FCSTD DOCUMENT  (FreeCAD 1.0R39285 (Git))
Label: Mover
License: All rights reserved
LicenseURL: https://en.wikipedia.org/wiki/All_rights_reserved
objects: App::Link×59, App::FeaturePython×47, Part::Feature×43, Part::FeaturePython×8, App::Part×4, Assembly::AssemblyLink×4, Assembly::JointGroup×2, Assembly::AssemblyObject×2, App::DocumentObjectGroup×1
note: 51 computed .brp shape members not serialized (recipe doc carries the construction recipe); baked Part::Feature solids carry a one-line shape summary decoded from their .brp
EXTERNAL_REF file=Heberteile.FCStd obj=Body001
EXTERNAL_REF file=Heberteile.FCStd obj=Body
EXTERNAL_REF file=Heberteile.FCStd obj=Body003
EXTERNAL_REF file=Heberteile.FCStd obj=Body002
EXTERNAL_REF file=Heberteile.FCStd obj=Body005
EXTERNAL_REF file=Heberteile.FCStd obj=Body006
EXTERNAL_REF file=Heberteile.FCStd obj=Body007

FEATURE [App::Link] B_Steppersledge_basic  label="B-Steppersledge basic"
  LinkPlacement = pos=(-30.1438,29,574.644) rot=(0.707107,0,-0.707107;3.14159rad)
  LinkedObject = -> <external Heberteile.FCStd>#Body001
  Placement = pos=(-30.1438,29,574.644) rot=(0.707107,0,-0.707107;3.14159rad)
FEATURE [App::Link] B_Steppersledge_Switch  label="B-Steppersledge Switch"
  LinkPlacement = pos=(30.8669,-32.6406,574.644) rot=(0,1,0;1.5708rad)
  LinkedObject = -> <external Heberteile.FCStd>#Body
  Placement = pos=(30.8669,-32.6406,574.644) rot=(0,1,0;1.5708rad)
FEATURE [App::Link] B_SlideBearing  label="B-Slide Bearing R"
  LinkPlacement = pos=(-29.9938,-1.19447e-11,401.144) rot=(-0.707107,0,0.707107;3.14159rad)
  LinkedObject = -> <external Heberteile.FCStd>#Body003
  Placement = pos=(-29.9938,-1.19447e-11,401.144) rot=(-0.707107,0,0.707107;3.14159rad)
FEATURE [App::Link] B_Sheetwasher  label="B-Mount Washer R"
  LinkPlacement = pos=(-26.1438,-3.388e-12,195.644) rot=(0.707107,0,-0.707107;3.14159rad)
  LinkedObject = -> <external Heberteile.FCStd>#Body002
  Placement = pos=(-26.1438,-3.388e-12,195.644) rot=(0.707107,0,-0.707107;3.14159rad)
FEATURE [Part::Feature] Part__Feature  label="23HS45-4204S"
  shape: bbox 1.354 x 20 x 1.354 mm, 4 faces (baked)
FEATURE [Part::Feature] Part__Feature001  label="23HS45-4204S001"
  shape: bbox 1.354 x 20 x 1.354 mm, 4 faces (baked)
FEATURE [Part::Feature] Part__Feature002  label="23HS45-4204S002"
  shape: bbox 1.354 x 20 x 1.354 mm, 4 faces (baked)
FEATURE [Part::Feature] Part__Feature003  label="23HS45-4204S003"
  shape: bbox 8 x 0.5 x 10.5 mm, 12 faces (baked)
FEATURE [Part::Feature] Part__Feature004  label="23HS45-4204S004"
  shape: bbox 57 x 78.2 x 137 mm, 432 faces (baked)
FEATURE [Part::Feature] Part__Feature005  label="23HS45-4204S005"
  shape: bbox 1.354 x 20 x 1.354 mm, 4 faces (baked)
FEATURE [App::Part] _3HS45_4204S  label="23HS45-4204S006"
  Group = -> [Part__Feature,Part__Feature001,Part__Feature002,Part__Feature003,Part__Feature004,Part__Feature005]
  Origin = -> Origin
FEATURE [Part::Feature] Part__Feature006  label="DM542T(V4.0)"
  shape: bbox 1.24 x 1.535 x 2.051 mm, 6 faces (baked)
FEATURE [Part::Feature] Part__Feature007  label="DM542T(V4.0)001"
  shape: bbox 6.47 x 10.45 x 10.4 mm, 69 faces (baked)
FEATURE [Part::Feature] Part__Feature008  label="DM542T(V4.0)002"
  shape: bbox 1.24 x 1.535 x 2.051 mm, 6 faces (baked)
FEATURE [Part::Feature] Part__Feature009  label="DM542T(V4.0)003"
  shape: bbox 19.2 x 10.45 x 10.4 mm, 168 faces (baked)
FEATURE [Part::Feature] Part__Feature010  label="DM542T(V4.0)004"
  shape: bbox 1.24 x 1.535 x 2.051 mm, 6 faces (baked)
FEATURE [Part::Feature] Part__Feature011  label="DM542T(V4.0)005"
  shape: bbox 24 x 13.06 x 13 mm, 168 faces (baked)
FEATURE [Part::Feature] Part__Feature012  label="DM542T(V4.0)006"
  shape: bbox 1.24 x 1.535 x 2.051 mm, 6 faces (baked)
FEATURE [Part::Feature] Part__Feature013  label="DM542T(V4.0)007"
  shape: bbox 1.24 x 1.535 x 2.051 mm, 6 faces (baked)
FEATURE [Part::Feature] Part__Feature014  label="DM542T(V4.0)008"
  shape: bbox 122 x 25.5 x 79.9 mm, 393 faces (baked)
FEATURE [App::Part] DM542T_V4_0_  label="DM542T(V4.0)009"
  Group = -> [Part__Feature006,Part__Feature007,Part__Feature008,Part__Feature009,Part__Feature010,Part__Feature011,Part__Feature012,Part__Feature013,Part__Feature014]
  Origin = -> Origin002
FEATURE [Part::Feature] Part__Feature016  label="Microswitch 20mm001"
  shape: bbox 3.3 x 1.3 x 2 mm, 8 faces (baked)
FEATURE [Part::Feature] Part__Feature017  label="Microswitch 20mm002"
  shape: bbox 4.6 x 9.15 x 18.7 mm, 30 faces (baked)
FEATURE [Part::Feature] Part__Feature018  label="Microswitch 20mm003"
  shape: bbox 3.1 x 3.6 x 0.5 mm, 9 faces (baked)
FEATURE [Part::Feature] Part__Feature019  label="Microswitch 20mm004"
  shape: bbox 3.1 x 3.6 x 0.5 mm, 9 faces (baked)
FEATURE [Part::Feature] Part__Feature020  label="Microswitch 20mm005"
  shape: bbox 3.1 x 3.6 x 0.5 mm, 9 faces (baked)
FEATURE [Part::Feature] Part__Feature021  label="Microswitch 20mm006"
  shape: bbox 3.4 x 4.979 x 4.979 mm, 6 faces (baked)
FEATURE [Part::Feature] Part__Feature022  label="base plate"
  Placement = pos=(40.6975,42.3791,107.628) rot=(0,0,1;0rad)
  shape: bbox 133.6 x 40.07 x 89.98 mm, 156 faces (baked)
FEATURE [Part::Feature] Part__Feature023  label="carrier plate"
  Placement = pos=(40.6975,172.684,107.628) rot=(0,0,1;3.14159rad)
  shape: bbox 64 x 43.47 x 38.95 mm, 106 faces (baked)
FEATURE [Part::Feature] Part__Feature024  label="upper lifting arm"
  Placement = pos=(123.841,140.552,107.628) rot=(0,0,1;2.8646rad)
  shape: bbox 166 x 65.79 x 28 mm, 172 faces (baked)
FEATURE [Part::Feature] Part__Feature025  label="top lifting arm"
  Placement = pos=(123.841,81.5103,107.628) rot=(-0.138054,0.990425,0;3.14159rad)
  shape: bbox 166 x 65.79 x 38 mm, 172 faces (baked)
FEATURE [Part::Feature] Part__Feature026  label="upper left lifting arm"
  Placement = pos=(-42.4461,140.552,107.628) rot=(0.990425,0.138054,0;3.14159rad)
  shape: bbox 165.5 x 66.16 x 28 mm, 206 faces (baked)
FEATURE [Part::Feature] Part__Feature027  label="top left lifting arm"
  Placement = pos=(-42.4461,81.5103,107.628) rot=(0,0,-1;0.276992rad)
  shape: bbox 165.5 x 66.16 x 38 mm, 206 faces (baked)
FEATURE [Part::Feature] Part__Feature028  label="top pins"
  Placement = pos=(27.4475,150.684,126.628) rot=(0.706529,-0.040404,-0.706529;3.22236rad)
  shape: bbox 11.83 x 11.83 x 46 mm, 15 faces (baked)
FEATURE [Part::Feature] Part__Feature029  label="bottom pins"
  Placement = pos=(27.4475,71.3791,131.628) rot=(-0.281558,0.917306,0.281558;1.657rad)
  shape: bbox 11.69 x 11.69 x 56 mm, 15 faces (baked)
FEATURE [Part::Feature] Part__Feature030  label="top pins001"
  Placement = pos=(53.9475,150.684,126.628) rot=(0.704441,0.086746,-0.704441;2.96853rad)
  shape: bbox 11.55 x 11.55 x 46 mm, 15 faces (baked)
FEATURE [Part::Feature] Part__Feature031  label="bottom pins001"
  Placement = pos=(53.9475,71.3791,131.628) rot=(0.632857,-0.446075,-0.632857;3.98076rad)
  shape: bbox 11.21 x 11.21 x 56 mm, 15 faces (baked)
FEATURE [Part::Feature] Part__Feature032  label="drive screw"
  Placement = pos=(-121.025,111.031,107.628) rot=(0.687636,-0.233053,0.687636;3.59952rad)
  shape: bbox 361.7 x 22.9 x 16.1 mm, 155 faces (baked)
FEATURE [Part::Feature] Part__Feature033  label="drive trunnion"
  Placement = pos=(202.42,111.031,107.628) rot=(0,-1,0;1.5708rad)
  shape: bbox 21.48 x 18 x 18 mm, 27 faces (baked)
FEATURE [Part::Feature] Part__Feature034  label="stationary trunnion"
  Placement = pos=(-103.025,111.031,107.628) rot=(0,-1,0;1.5708rad)
  shape: bbox 18 x 18 x 18 mm, 14 faces (baked)
FEATURE [Part::Feature] Part__Feature035  label="turunnion pins"
  Placement = pos=(-112.025,111.031,126.628) rot=(-0.675166,0.297157,0.675166;2.5639rad)
  shape: bbox 15 x 15 x 16 mm, 9 faces (baked)
FEATURE [Part::Feature] Part__Feature036  label="turunnion pins001"
  Placement = pos=(-112.025,111.031,88.6277) rot=(-0.079144,-0.993716,-0.079144;1.5771rad)
  shape: bbox 15 x 15 x 16 mm, 9 faces (baked)
FEATURE [Part::Feature] Part__Feature037  label="turunnion pins002"
  Placement = pos=(193.42,111.031,88.6277) rot=(-0.079144,-0.993716,-0.079144;1.5771rad)
  shape: bbox 15 x 15 x 16 mm, 9 faces (baked)
FEATURE [Part::Feature] Part__Feature038  label="turunnion pins003"
  Placement = pos=(193.42,111.031,126.628) rot=(0.706974,-0.019411,-0.706974;3.18041rad)
  shape: bbox 15 x 15 x 16 mm, 9 faces (baked)
FEATURE [Part::Feature] Part__Feature039  label="snap ring"
  Placement = pos=(53.9475,150.684,87.8777) rot=(0,0,-1;0.735498rad)
  shape: bbox 10.43 x 10.13 x 0.5 mm, 22 faces (baked)
FEATURE [Part::Feature] Part__Feature040  label="snap ring001"
  Placement = pos=(27.4475,150.684,87.8777) rot=(0,0,-1;0.735498rad)
  shape: bbox 10.43 x 10.13 x 0.5 mm, 22 faces (baked)
FEATURE [Part::Feature] Part__Feature041  label="snap ring002"
  Placement = pos=(53.9475,71.3791,83.3777) rot=(0.933139,-0.359516,0;3.14159rad)
  shape: bbox 10.43 x 10.13 x 0.5 mm, 22 faces (baked)
FEATURE [Part::Feature] Part__Feature042  label="snap ring003"
  Placement = pos=(27.4475,71.3791,82.8777) rot=(0,0,-1;0.735498rad)
  shape: bbox 10.43 x 10.13 x 0.5 mm, 22 faces (baked)
FEATURE [App::Part] lifting_jack_assembley  label="lifting jack assembley"
  Group = -> [Part__Feature022,Part__Feature023,Part__Feature024,Part__Feature025,Part__Feature026,Part__Feature027,Part__Feature028,Part__Feature029,Part__Feature030,Part__Feature031,Part__Feature032,Part__Feature033,Part__Feature034,Part__Feature035,Part__Feature036,Part__Feature037,Part__Feature038,Part__Feature039,Part__Feature040,Part__Feature041,Part__Feature042]
  Origin = -> Origin004
  Placement = pos=(267.1,-82.7,87.3) rot=(0,-1,0;3.14159rad)
FEATURE [App::Link] _3HS45_4204S006  label="23HS45-4204S007"
  LinkedObject = -> _3HS45_4204S
FEATURE [App::FeaturePython] GroundedJoint  # Assembly grounded joint (typed FeaturePython)
  ObjectToGround = -> _3HS45_4204S006
FEATURE [App::FeaturePython] Joint  label="Distance"  # Assembly joint (typed FeaturePython)
  Activated = true
  AngleMax = 0
  AngleMin = 0
  Detach1 = false
  Detach2 = false
  Distance = 0
  Distance2 = 0
  EnableAngleMax = false
  EnableAngleMin = false
  EnableLengthMax = false
  EnableLengthMin = false
  JointType = 5 (Distance)
  LengthMax = 0
  LengthMin = 0
  Placement1 = pos=(461.644,29,-11.5732) rot=(0,1,0;1.5708rad)
  Placement2 = pos=(-0.00133091,0.00678875,113) rot=(0,0,1;0rad)
  Reference1 = -> Assembly [B_Steppersledge_Switch.Face43,B_Steppersledge_Switch.Face43]
  Reference2 = -> Assembly [_3HS45_4204S006.Part__Feature004.Face286,_3HS45_4204S006.Part__Feature004.Vertex39]
FEATURE [App::FeaturePython] Joint001  label="Distance001"  # Assembly joint (typed FeaturePython)
  Activated = true
  AngleMax = 0
  AngleMin = 0
  Detach1 = false
  Detach2 = false
  Distance = 0
  Distance2 = 0
  EnableAngleMax = false
  EnableAngleMin = false
  EnableLengthMax = false
  EnableLengthMin = false
  JointType = 5 (Distance)
  LengthMax = 0
  LengthMin = 0
  Placement1 = pos=(-0.00133091,0.00678875,113) rot=(0,0,1;0rad)
  Placement2 = pos=(461.644,29,-11.5732) rot=(0,1,0;1.5708rad)
  Reference1 = -> Assembly [_3HS45_4204S006.Part__Feature004.Face286,_3HS45_4204S006.Part__Feature004.Vertex48]
  Reference2 = -> Assembly [B_Steppersledge_basic.Face51,B_Steppersledge_basic.Face51]
FEATURE [App::FeaturePython] Joint002  label="Slider"  # Assembly joint (typed FeaturePython)
  Activated = true
  AngleMax = 0
  AngleMin = 0
  Detach1 = false
  Detach2 = false
  Distance = 0
  Distance2 = 0
  EnableAngleMax = false
  EnableAngleMin = false
  EnableLengthMax = false
  EnableLengthMin = false
  JointType = 3 (Slider)
  LengthMax = 0
  LengthMin = 0
  Placement1 = pos=(-23.57,-23.57,110.25) rot=(0,0,1;0rad)
  Placement2 = pos=(460.644,52.57,-6.57381) rot=(0,1,0;1.5708rad)
  Reference1 = -> Assembly [_3HS45_4204S006.Part__Feature004.Face20,_3HS45_4204S006.Part__Feature004.Face20]
  Reference2 = -> Assembly [B_Steppersledge_basic.Face48,B_Steppersledge_basic.Face48]
FEATURE [App::FeaturePython] Joint003  label="Slider001"  # Assembly joint (typed FeaturePython)
  Activated = true
  AngleMax = 0
  AngleMin = 0
  Detach1 = false
  Detach2 = false
  Distance = 0
  Distance2 = 0
  EnableAngleMax = false
  EnableAngleMin = false
  EnableLengthMax = false
  EnableLengthMin = false
  JointType = 3 (Slider)
  LengthMax = 0
  LengthMin = 0
  Placement1 = pos=(459.644,5.43,-6.57381) rot=(0,1,0;1.5708rad)
  Placement2 = pos=(-23.57,23.57,110.25) rot=(0,0,1;0rad)
  Reference1 = -> Assembly [B_Steppersledge_basic.Edge90,B_Steppersledge_basic.Edge90]
  Reference2 = -> Assembly [_3HS45_4204S006.Part__Feature004.Face23,_3HS45_4204S006.Part__Feature004.Face23]
FEATURE [App::FeaturePython] Joint004  label="Slider002"  # Assembly joint (typed FeaturePython)
  Activated = true
  AngleMax = 0
  AngleMin = 0
  Detach1 = false
  Detach2 = false
  Distance = 0
  Distance2 = 0
  EnableAngleMax = false
  EnableAngleMin = false
  EnableLengthMax = false
  EnableLengthMin = false
  JointType = 3 (Slider)
  LengthMax = 0
  LengthMin = 0
  Placement1 = pos=(460.644,52.57,-6.57381) rot=(0,1,0;1.5708rad)
  Placement2 = pos=(23.57,23.57,110.25) rot=(0,0,1;0rad)
  Reference1 = -> Assembly [B_Steppersledge_Switch.Face64,B_Steppersledge_Switch.Face64]
  Reference2 = -> Assembly [_3HS45_4204S006.Part__Feature004.Face22,_3HS45_4204S006.Part__Feature004.Face22]
FEATURE [App::FeaturePython] Joint005  label="Slider003"  # Assembly joint (typed FeaturePython)
  Activated = true
  AngleMax = 0
  AngleMin = 0
  Detach1 = false
  Detach2 = false
  Distance = 0
  Distance2 = 0
  EnableAngleMax = false
  EnableAngleMin = false
  EnableLengthMax = false
  EnableLengthMin = false
  JointType = 3 (Slider)
  LengthMax = 0
  LengthMin = 0
  Placement1 = pos=(23.57,-23.57,110.25) rot=(0,0,1;0rad)
  Placement2 = pos=(460.644,5.43,-6.57381) rot=(0,1,0;1.5708rad)
  Reference1 = -> Assembly [_3HS45_4204S006.Part__Feature004.Face21,_3HS45_4204S006.Part__Feature004.Face21]
  Reference2 = -> Assembly [B_Steppersledge_Switch.Face63,B_Steppersledge_Switch.Face63]
FEATURE [Part::FeaturePython] Nut  label="M5-Mutter"  # WARN: FeaturePython — macro-defined, semantics opaque (R4)
  Diameter = 1
  Invert = false
  LeftHanded = false
  MatchOuter = false
  OffsetAngle = 0
  Placement = pos=(-12.9,0,-58.2) rot=(0,0,1;0rad)
  Thread = false
  Type = 33
FEATURE [Part::FeaturePython] Nut001  label="M2.5-Mutter"  # WARN: FeaturePython — macro-defined, semantics opaque (R4)
  Diameter = 3
  Invert = false
  LeftHanded = false
  MatchOuter = false
  OffsetAngle = 0
  Placement = pos=(0,0,-57.3) rot=(0,0,1;0rad)
  Thread = false
  Type = 31
FEATURE [Part::FeaturePython] Washer  label="M5-Scheibe"  # WARN: FeaturePython — macro-defined, semantics opaque (R4)
  Diameter = 6
  Invert = false
  MatchOuter = false
  OffsetAngle = 0
  Placement = pos=(-12.4,0,-51.8) rot=(0,0,1;0rad)
  Type = 8
FEATURE [Part::FeaturePython] Washer001  label="M2.5-Scheibe"  # WARN: FeaturePython — macro-defined, semantics opaque (R4)
  Diameter = 3
  Invert = false
  MatchOuter = false
  OffsetAngle = 0
  Placement = pos=(0,0,-51.5) rot=(0,0,1;0rad)
  Type = 8
FEATURE [Part::FeaturePython] Screw003  label="M5x12-Schraube"  # WARN: FeaturePython — macro-defined, semantics opaque (R4)
  Diameter = 5
  Invert = false
  LeftHanded = false
  Length = 2
  LengthCustom = 12
  MatchOuter = false
  OffsetAngle = 0
  Placement = pos=(-13.1,0,-36.9) rot=(0,0,1;0rad)
  Thread = false
  Type = 53
FEATURE [App::Link] M5x12_Schraube  label="M5x12-Schraube-Stepper-001"
  LinkPlacement = pos=(-23.57,23.57,108) rot=(1,0,0;3.14159rad)
  LinkedObject = -> Screw003
  Placement = pos=(-23.57,23.57,108) rot=(1,0,0;3.14159rad)
FEATURE [App::Link] M5x12_Schraube001  label="M5x12-Schraube-Stepper-002"
  LinkPlacement = pos=(23.57,23.57,108) rot=(1,0,0;3.14159rad)
  LinkedObject = -> Screw003
  Placement = pos=(23.57,23.57,108) rot=(1,0,0;3.14159rad)
FEATURE [App::Link] M5x12_Schraube002  label="M5x12-Schraube-Stepper-003"
  LinkPlacement = pos=(23.57,-23.57,108) rot=(1,0,0;3.14159rad)
  LinkedObject = -> Screw003
  Placement = pos=(23.57,-23.57,108) rot=(1,0,0;3.14159rad)
FEATURE [App::Link] M5x12_Schraube003  label="M5x12-Schraube-Stepper-004"
  LinkPlacement = pos=(-23.57,-23.57,108) rot=(1,0,0;3.14159rad)
  LinkedObject = -> Screw003
  Placement = pos=(-23.57,-23.57,108) rot=(1,0,0;3.14159rad)
FEATURE [App::Link] M5_Scheibe  label="M5-Scheibe-Stepper-001"
  LinkPlacement = pos=(-23.57,23.57,115) rot=(0,0,1;0rad)
  LinkedObject = -> Washer
  Placement = pos=(-23.57,23.57,115) rot=(0,0,1;0rad)
FEATURE [App::Link] M5_Scheibe001  label="M5-Scheibe-Stepper-003"
  LinkPlacement = pos=(23.57,-23.57,115) rot=(0,0,1;3.14159rad)
  LinkedObject = -> Washer
  Placement = pos=(23.57,-23.57,115) rot=(0,0,1;3.14159rad)
FEATURE [App::Link] M5_Scheibe002  label="M5-Scheibe-Stepper-002"
  LinkPlacement = pos=(23.57,23.57,115) rot=(0,0,1;3.14159rad)
  LinkedObject = -> Washer
  Placement = pos=(23.57,23.57,115) rot=(0,0,1;3.14159rad)
FEATURE [App::Link] M5_Scheibe003  label="M5-Scheibe-Stepper-004"
  LinkPlacement = pos=(-23.57,-23.57,115) rot=(0,0,1;0rad)
  LinkedObject = -> Washer
  Placement = pos=(-23.57,-23.57,115) rot=(0,0,1;0rad)
FEATURE [App::Link] M5_Scheibe006  label="M5-Scheibe-Jack-001"
  LinkPlacement = pos=(33.1438,-3.5877e-12,195.644) rot=(-0.707107,0,0.707107;3.14159rad)
  LinkedObject = -> Washer
  Placement = pos=(33.1438,-3.5877e-12,195.644) rot=(-0.707107,0,0.707107;3.14159rad)
FEATURE [App::Link] M5_Scheibe007  label="M5-Scheibe-Jack-002"
  LinkPlacement = pos=(-32.1438,-3.4094e-12,195.644) rot=(0.707107,0,-0.707107;3.14159rad)
  LinkedObject = -> Washer
  Placement = pos=(-32.1438,-3.4094e-12,195.644) rot=(0.707107,0,-0.707107;3.14159rad)
FEATURE [App::Link] M5_Mutter  label="M5-Mutter-Stepper-001"
  LinkPlacement = pos=(-23.57,23.57,116) rot=(0,0,1;0rad)
  LinkedObject = -> Nut
  Placement = pos=(-23.57,23.57,116) rot=(0,0,1;0rad)
FEATURE [App::Link] M5_Mutter001  label="M5-Mutter-Stepper-002"
  LinkPlacement = pos=(23.57,23.57,116) rot=(0,0,1;3.14159rad)
  LinkedObject = -> Nut
  Placement = pos=(23.57,23.57,116) rot=(0,0,1;3.14159rad)
FEATURE [App::Link] M5_Mutter002  label="M5-Mutter-Stepper-003"
  LinkPlacement = pos=(23.57,-23.57,116) rot=(0,0,1;3.14159rad)
  LinkedObject = -> Nut
  Placement = pos=(23.57,-23.57,116) rot=(0,0,1;3.14159rad)
FEATURE [App::Link] M5_Mutter003  label="M5-Mutter-Stepper-004"
  LinkPlacement = pos=(-23.57,-23.57,116) rot=(0,0,1;0rad)
  LinkedObject = -> Nut
  Placement = pos=(-23.57,-23.57,116) rot=(0,0,1;0rad)
FEATURE [App::FeaturePython] Joint006  label="Gleitverbindung"  # Assembly joint (typed FeaturePython)
  Activated = true
  AngleMax = 0
  AngleMin = 0
  Detach1 = false
  Detach2 = false
  Distance = 0
  Distance2 = 0
  EnableAngleMax = false
  EnableAngleMin = false
  EnableLengthMax = false
  EnableLengthMin = false
  JointType = 3 (Slider)
  LengthMax = 0
  LengthMin = 0
  Placement1 = pos=(-23.57,23.57,108) rot=(0,0,1;0rad)
  Reference1 = -> Assembly [_3HS45_4204S006.Part__Feature004.Edge765,_3HS45_4204S006.Part__Feature004.Edge765]
  Reference2 = -> Assembly [M5x12_Schraube.Edge50,M5x12_Schraube.Edge50]
FEATURE [App::FeaturePython] Joint007  label="Gleitverbindung001"  # Assembly joint (typed FeaturePython)
  Activated = true
  AngleMax = 0
  AngleMin = 0
  Detach1 = false
  Detach2 = false
  Distance = 0
  Distance2 = 0
  EnableAngleMax = false
  EnableAngleMin = false
  EnableLengthMax = false
  EnableLengthMin = false
  JointType = 3 (Slider)
  LengthMax = 0
  LengthMin = 0
  Placement2 = pos=(459.644,5.43,-6.57381) rot=(0,1,0;1.5708rad)
  Reference1 = -> Assembly [M5_Scheibe.Edge5,M5_Scheibe.Edge5]
  Reference2 = -> Assembly [B_Steppersledge_basic.Edge90,B_Steppersledge_basic.Edge90]
FEATURE [App::FeaturePython] Joint008  label="Gleitverbindung002"  # Assembly joint (typed FeaturePython)
  Activated = true
  AngleMax = 0
  AngleMin = 0
  Detach1 = false
  Detach2 = false
  Distance = 0
  Distance2 = 0
  EnableAngleMax = false
  EnableAngleMin = false
  EnableLengthMax = false
  EnableLengthMin = false
  JointType = 3 (Slider)
  LengthMax = 0
  LengthMin = 0
  Placement2 = pos=(0,0,1) rot=(0,0,1;0rad)
  Reference1 = -> Assembly [M5_Mutter.Edge27,M5_Mutter.Edge27]
  Reference2 = -> Assembly [M5_Scheibe.Edge1,M5_Scheibe.Edge1]
FEATURE [App::FeaturePython] Joint009  label="Gleitverbindung003"  # Assembly joint (typed FeaturePython)
  Activated = true
  AngleMax = 0
  AngleMin = 0
  Detach1 = false
  Detach2 = false
  Distance = 0
  Distance2 = 0
  EnableAngleMax = false
  EnableAngleMin = false
  EnableLengthMax = false
  EnableLengthMin = false
  JointType = 3 (Slider)
  LengthMax = 0
  LengthMin = 0
  Placement2 = pos=(23.57,23.57,108) rot=(0,0,1;0rad)
  Reference1 = -> Assembly [M5x12_Schraube001.Edge50,M5x12_Schraube001.Edge50]
  Reference2 = -> Assembly [_3HS45_4204S006.Part__Feature004.Edge752,_3HS45_4204S006.Part__Feature004.Edge752]
FEATURE [App::FeaturePython] Joint012  label="Gleitverbindung006"  # Assembly joint (typed FeaturePython)
  Activated = true
  AngleMax = 0
  AngleMin = 0
  Detach1 = false
  Detach2 = false
  Distance = 0
  Distance2 = 0
  EnableAngleMax = false
  EnableAngleMin = false
  EnableLengthMax = false
  EnableLengthMin = false
  JointType = 3 (Slider)
  LengthMax = 0
  LengthMin = 0
  Placement1 = pos=(23.57,-23.57,108) rot=(0,0,1;0rad)
  Reference1 = -> Assembly [_3HS45_4204S006.Part__Feature004.Edge711,_3HS45_4204S006.Part__Feature004.Edge711]
  Reference2 = -> Assembly [M5x12_Schraube002.Edge50,M5x12_Schraube002.Edge50]
FEATURE [App::FeaturePython] Joint013  label="Gleitverbindung007"  # Assembly joint (typed FeaturePython)
  Activated = true
  AngleMax = 0
  AngleMin = 0
  Detach1 = false
  Detach2 = false
  Distance = 0
  Distance2 = 0
  EnableAngleMax = false
  EnableAngleMin = false
  EnableLengthMax = false
  EnableLengthMin = false
  JointType = 3 (Slider)
  LengthMax = 0
  LengthMin = 0
  Placement1 = pos=(459.644,5.43,-6.57381) rot=(0,1,0;1.5708rad)
  Reference1 = -> Assembly [B_Steppersledge_Switch.Edge171,B_Steppersledge_Switch.Edge171]
  Reference2 = -> Assembly [M5_Scheibe001.Edge5,M5_Scheibe001.Edge5]
FEATURE [App::FeaturePython] Joint014  label="Gleitverbindung008"  # Assembly joint (typed FeaturePython)
  Activated = true
  AngleMax = 0
  AngleMin = 0
  Detach1 = false
  Detach2 = false
  Distance = 0
  Distance2 = 0
  EnableAngleMax = false
  EnableAngleMin = false
  EnableLengthMax = false
  EnableLengthMin = false
  JointType = 3 (Slider)
  LengthMax = 0
  LengthMin = 0
  Placement1 = pos=(0,0,1) rot=(0,0,1;0rad)
  Reference1 = -> Assembly [M5_Scheibe001.Edge1,M5_Scheibe001.Edge1]
  Reference2 = -> Assembly [M5_Mutter002.Edge27,M5_Mutter002.Edge27]
FEATURE [App::FeaturePython] Joint015  label="Gleitverbindung009"  # Assembly joint (typed FeaturePython)
  Activated = true
  AngleMax = 0
  AngleMin = 0
  Detach1 = false
  Detach2 = false
  Distance = 0
  Distance2 = 0
  EnableAngleMax = false
  EnableAngleMin = false
  EnableLengthMax = false
  EnableLengthMin = false
  JointType = 3 (Slider)
  LengthMax = 0
  LengthMin = 0
  Placement1 = pos=(-23.57,-23.57,108) rot=(0,0,1;0rad)
  Reference1 = -> Assembly [_3HS45_4204S006.Part__Feature004.Edge79,_3HS45_4204S006.Part__Feature004.Edge79]
  Reference2 = -> Assembly [M5x12_Schraube003.Edge50,M5x12_Schraube003.Edge50]
FEATURE [App::FeaturePython] Joint016  label="Gleitverbindung010"  # Assembly joint (typed FeaturePython)
  Activated = true
  AngleMax = 0
  AngleMin = 0
  Detach1 = false
  Detach2 = false
  Distance = 0
  Distance2 = 0
  EnableAngleMax = false
  EnableAngleMin = false
  EnableLengthMax = false
  EnableLengthMin = false
  JointType = 3 (Slider)
  LengthMax = 0
  LengthMin = 0
  Placement1 = pos=(459.644,52.57,-6.57381) rot=(0,1,0;1.5708rad)
  Reference1 = -> Assembly [B_Steppersledge_basic.Edge91,B_Steppersledge_basic.Edge91]
  Reference2 = -> Assembly [M5_Scheibe003.Edge5,M5_Scheibe003.Edge5]
FEATURE [App::FeaturePython] Joint017  label="Gleitverbindung011"  # Assembly joint (typed FeaturePython)
  Activated = true
  AngleMax = 0
  AngleMin = 0
  Detach1 = false
  Detach2 = false
  Distance = 0
  Distance2 = 0
  EnableAngleMax = false
  EnableAngleMin = false
  EnableLengthMax = false
  EnableLengthMin = false
  JointType = 3 (Slider)
  LengthMax = 0
  LengthMin = 0
  Placement1 = pos=(0,0,1) rot=(0,0,1;0rad)
  Reference1 = -> Assembly [M5_Scheibe003.Edge1,M5_Scheibe003.Edge1]
  Reference2 = -> Assembly [M5_Mutter003.Edge27,M5_Mutter003.Edge27]
FEATURE [App::Link] M5x12_Schraube004  label="M5x16-Schraube-Jack-001"
  LinkPlacement = pos=(33.1438,-3.5877e-12,195.644) rot=(0,1,0;1.5708rad)
  LinkedObject = -> Screw004
  Placement = pos=(33.1438,-3.5877e-12,195.644) rot=(0,1,0;1.5708rad)
FEATURE [App::Link] M5x12_Schraube005  label="M5x16-Schraube-Jack-002"
  LinkPlacement = pos=(-33.1438,-3.413e-12,195.644) rot=(0.707107,0,-0.707107;3.14159rad)
  LinkedObject = -> Screw004
  Placement = pos=(-33.1438,-3.413e-12,195.644) rot=(0.707107,0,-0.707107;3.14159rad)
FEATURE [App::FeaturePython] Joint018  label="Gleitverbindung012"  # Assembly joint (typed FeaturePython)
  Activated = true
  AngleMax = 0
  AngleMin = 0
  Detach1 = false
  Detach2 = false
  Distance = 0
  Distance2 = 0
  EnableAngleMax = false
  EnableAngleMin = false
  EnableLengthMax = false
  EnableLengthMin = false
  JointType = 3 (Slider)
  LengthMax = 0
  LengthMin = 0
  Placement1 = pos=(379,29,2) rot=(0,0,1;0rad)
  Placement2 = pos=(0,0,1) rot=(0,0,1;0rad)
  Reference1 = -> Assembly [B_Steppersledge_Switch.Edge26,B_Steppersledge_Switch.Edge26]
  Reference2 = -> Assembly [M5_Scheibe006.Edge1,M5_Scheibe006.Edge1]
FEATURE [App::FeaturePython] Joint019  label="Gleitverbindung013"  # Assembly joint (typed FeaturePython)
  Activated = true
  AngleMax = 0
  AngleMin = 0
  Detach1 = false
  Detach2 = false
  Distance = 0
  Distance2 = 0
  EnableAngleMax = false
  EnableAngleMin = false
  EnableLengthMax = false
  EnableLengthMin = false
  JointType = 3 (Slider)
  LengthMax = 0
  LengthMin = 0
  Reference1 = -> Assembly [M5_Scheibe006.Edge5,M5_Scheibe006.Edge5]
  Reference2 = -> Assembly [M5x12_Schraube004.Edge50,M5x12_Schraube004.Edge50]
FEATURE [App::FeaturePython] Joint020  label="Gleitverbindung014"  # Assembly joint (typed FeaturePython)
  Activated = true
  AngleMax = 0
  AngleMin = 0
  Detach1 = false
  Detach2 = false
  Distance = 0
  Distance2 = 0
  EnableAngleMax = false
  EnableAngleMin = false
  EnableLengthMax = false
  EnableLengthMin = false
  JointType = 3 (Slider)
  LengthMax = 0
  LengthMin = 0
  Placement1 = pos=(379,29,2) rot=(0,0,1;0rad)
  Reference1 = -> Assembly [B_Steppersledge_basic.Edge63,B_Steppersledge_basic.Edge63]
  Reference2 = -> Assembly [M5_Scheibe007.Edge5,M5_Scheibe007.Edge5]
FEATURE [App::FeaturePython] Joint021  label="Gleitverbindung015"  # Assembly joint (typed FeaturePython)
  Activated = true
  AngleMax = 0
  AngleMin = 0
  Detach1 = false
  Detach2 = false
  Distance = 0
  Distance2 = 0
  EnableAngleMax = false
  EnableAngleMin = false
  EnableLengthMax = false
  EnableLengthMin = false
  JointType = 3 (Slider)
  LengthMax = 0
  LengthMin = 0
  Placement1 = pos=(0,0,1) rot=(0,0,1;0rad)
  Reference1 = -> Assembly [M5_Scheibe007.Edge1,M5_Scheibe007.Edge1]
  Reference2 = -> Assembly [M5x12_Schraube005.Edge50,M5x12_Schraube005.Edge50]
FEATURE [App::Link] Microswitch_20mm007  label="Microswitch"
  LinkPlacement = pos=(54.0665,25.4004,278.902) rot=(-0.002003,-0.001876,0.999996;1.57097rad)
  LinkedObject = -> Microswitch_20mm
  Placement = pos=(54.0665,25.4004,278.902) rot=(-0.002003,-0.001876,0.999996;1.57097rad)
FEATURE [Part::FeaturePython] Screw  label="M2.5x16-Schraube"  # WARN: FeaturePython — macro-defined, semantics opaque (R4)
  Diameter = 2
  Invert = false
  LeftHanded = false
  Length = 4
  LengthCustom = 16
  MatchOuter = false
  OffsetAngle = 0
  Placement = pos=(16.2,0,-58.5) rot=(0,0,1;0rad)
  Thread = false
  Type = 51
FEATURE [App::Link] M2_5x12_Schraube  label="M2.5x16-Schraube001"
  LinkPlacement = pos=(51.8225,34.8981,264.042) rot=(0.014493,0.707079,0.706986;3.17082rad)
  LinkedObject = -> Screw
  Placement = pos=(51.8225,34.8981,264.042) rot=(0.014493,0.707079,0.706986;3.17082rad)
FEATURE [App::Link] M2_5_Mutter  label="M2.5-Mutter001"
  LinkPlacement = pos=(51.7878,19.7993,273.644) rot=(-0.576113,0.577955,0.577981;2.09651rad)
  LinkedObject = -> Nut001
  Placement = pos=(51.7878,19.7993,273.644) rot=(-0.576113,0.577955,0.577981;2.09651rad)
FEATURE [App::Link] M2_5x12_Schraube001  label="M2.5x16-Schraube002"
  LinkPlacement = pos=(51.7852,34.8993,273.642) rot=(0,0.707152,0.707062;3.14184rad)
  LinkedObject = -> Screw
  Placement = pos=(51.7852,34.8993,273.642) rot=(0,0.707152,0.707062;3.14184rad)
FEATURE [App::Link] M2_5_Mutter001  label="M2.5-Mutter002"
  LinkPlacement = pos=(51.7873,21.7981,264.144) rot=(0.936105,-0.248607,0.248801;1.6367rad)
  LinkedObject = -> Nut001
  Placement = pos=(51.7873,21.7981,264.144) rot=(0.936105,-0.248607,0.248801;1.6367rad)
FEATURE [Part::Feature] Part__Feature015  label="Microswitch 20mm"
  shape: bbox 53.34 x 10.88 x 20.15 mm, 272 faces (baked)
FEATURE [App::Part] Microswitch_20mm  label="Microswitch 20mm007"
  Group = -> [Part__Feature015,Part__Feature016,Part__Feature017,Part__Feature018,Part__Feature019,Part__Feature020,Part__Feature021]
  Origin = -> Origin003
FEATURE [App::Link] B_Slide_Bearing_Wascher  label="B-Slide Bearing Wascher R"
  LinkPlacement = pos=(-26.0938,-1.19325e-11,401.144) rot=(-0.707107,0,0.707107;3.14159rad)
  LinkedObject = -> <external Heberteile.FCStd>#Body005
  Placement = pos=(-26.0938,-1.19325e-11,401.144) rot=(-0.707107,0,0.707107;3.14159rad)
FEATURE [App::Link] B_Slide_Bearing_Wascher001  label="B-Slide Bearing Wascher L"
  LinkPlacement = pos=(26.0938,-1.63222e-11,401.144) rot=(0.707107,0,0.707107;3.14159rad)
  LinkedObject = -> <external Heberteile.FCStd>#Body005
  Placement = pos=(26.0938,-1.63222e-11,401.144) rot=(0.707107,0,0.707107;3.14159rad)
FEATURE [App::Link] B_Mount_Washer  label="B-Mount Washer L"
  LinkPlacement = pos=(30.1438,-3.5981e-12,195.644) rot=(-0.707107,0,0.707107;3.14159rad)
  LinkedObject = -> <external Heberteile.FCStd>#Body002
  Placement = pos=(30.1438,-3.5981e-12,195.644) rot=(-0.707107,0,0.707107;3.14159rad)
FEATURE [App::FeaturePython] Joint052  label="Mount01"  # Assembly joint (typed FeaturePython)
  Activated = true
  AngleMax = 0
  AngleMin = 0
  Detach1 = false
  Detach2 = false
  Distance = 0
  Distance2 = 0
  EnableAngleMax = false
  EnableAngleMin = false
  EnableLengthMax = false
  EnableLengthMin = false
  JointType = 3 (Slider)
  LengthMax = 0
  LengthMin = 0
  Placement1 = pos=(379,29,0) rot=(0,0,1;0rad)
  Placement2 = pos=(0,0,4) rot=(0,0,1;0rad)
  Reference1 = -> Assembly [B_Steppersledge_basic.Edge19,B_Steppersledge_basic.Edge19]
  Reference2 = -> Assembly [B_Sheetwasher.Edge6,B_Sheetwasher.Edge6]
FEATURE [App::FeaturePython] Joint053  label="Gleitverbindung047"  # Assembly joint (typed FeaturePython)
  Activated = true
  AngleMax = 0
  AngleMin = 0
  Detach1 = false
  Detach2 = false
  Distance = 0
  Distance2 = 0
  EnableAngleMax = false
  EnableAngleMin = false
  EnableLengthMax = false
  EnableLengthMin = false
  JointType = 3 (Slider)
  LengthMax = 0
  LengthMin = 0
  Placement1 = pos=(379,29,3.6e-15) rot=(0,0,1;0rad)
  Reference1 = -> Assembly [B_Steppersledge_Switch.Edge90,B_Steppersledge_Switch.Edge90]
  Reference2 = -> Assembly [B_Mount_Washer.Edge5,B_Mount_Washer.Edge5]
FEATURE [Part::FeaturePython] Screw004  label="M5x16-Schraube"  # WARN: FeaturePython — macro-defined, semantics opaque (R4)
  Diameter = 5
  Invert = false
  LeftHanded = false
  Length = 3
  LengthCustom = 16
  MatchOuter = false
  OffsetAngle = 0
  Placement = pos=(-3.5,0,-36.9) rot=(0,0,1;0rad)
  Thread = false
  Type = 53
FEATURE [Part::FeaturePython] Screw005  label="M5x20-Schraube"  # WARN: FeaturePython — macro-defined, semantics opaque (R4)
  Diameter = 5
  Invert = false
  LeftHanded = false
  Length = 4
  LengthCustom = 20
  MatchOuter = false
  OffsetAngle = 0
  Placement = pos=(-3.5,0,-36.9) rot=(0,0,1;0rad)
  Thread = false
  Type = 53
FEATURE [App::Link] B_Slide_Bearing_w__Indicator  label="B-Slide Bearing w. Indicator L"
  LinkPlacement = pos=(29.9938,-1.63076e-11,401.144) rot=(0.707107,0,0.707107;3.14159rad)
  LinkedObject = -> <external Heberteile.FCStd>#Body006
  Placement = pos=(29.9938,-1.63076e-11,401.144) rot=(0.707107,0,0.707107;3.14159rad)
FEATURE [App::FeaturePython] Joint056  label="ZylindrischeVerbindung"  # Assembly joint (typed FeaturePython)
  Activated = true
  AngleMax = 0
  AngleMin = 0
  Detach1 = false
  Detach2 = false
  Distance = 0
  Distance2 = 0
  EnableAngleMax = false
  EnableAngleMin = false
  EnableLengthMax = false
  EnableLengthMin = false
  JointType = 2 (Cylindrical)
  LengthMax = 0
  LengthMin = 0
  Offset1 = pos=(0,0,0.3) rot=(0,0,1;0rad)
  Placement1 = pos=(173.5,21.3,1) rot=(-1,0,0;1.5708rad)
  Placement2 = pos=(0,-7.7,1.15) rot=(1,0,0;4.71239rad)
  Reference1 = -> Assembly [B_Steppersledge_basic.Face17,B_Steppersledge_basic.Face17]
  Reference2 = -> Assembly [B_SlideBearing.Face18,B_SlideBearing.Face18]
FEATURE [App::FeaturePython] Joint057  label="Parallel"  # Assembly joint (typed FeaturePython)
  Activated = true
  AngleMax = 0
  AngleMin = 0
  Detach1 = false
  Detach2 = false
  Distance = 0
  Distance2 = 0
  EnableAngleMax = false
  EnableAngleMin = false
  EnableLengthMax = false
  EnableLengthMin = false
  JointType = 6 (Parallel)
  LengthMax = 0
  LengthMin = 0
  Placement1 = pos=(0,-7.7,-3.6e-15) rot=(0.707107,0,0.707107;3.14159rad)
  Placement2 = pos=(173.5,21,0) rot=(0.707107,0,0.707107;3.14159rad)
  Reference1 = -> Assembly [B_SlideBearing.Edge47,B_SlideBearing.Edge47]
  Reference2 = -> Assembly [B_Steppersledge_basic.Edge17,B_Steppersledge_basic.Edge17]
FEATURE [App::FeaturePython] Joint061  label="Gleitverbindung053"  # Assembly joint (typed FeaturePython)
  Activated = true
  AngleMax = 0
  AngleMin = 0
  Detach1 = false
  Detach2 = false
  Distance = 0
  Distance2 = 0
  EnableAngleMax = false
  EnableAngleMin = false
  EnableLengthMax = false
  EnableLengthMin = false
  JointType = 3 (Slider)
  LengthMax = 0
  LengthMin = 0
  Offset1 = pos=(0,0,-0.3) rot=(0,0,1;0rad)
  Offset2 = pos=(0,0,0) rot=(0,0,1;3.14159rad)
  Placement1 = pos=(0,-8,1.15) rot=(-1,0,0;1.5708rad)
  Placement2 = pos=(173.5,37,1) rot=(0,0.707107,0.707107;3.14159rad)
  Reference1 = -> Assembly [B_Slide_Bearing_w__Indicator.Face2,B_Slide_Bearing_w__Indicator.Face2]
  Reference2 = -> Assembly [B_Steppersledge_Switch.Face21,B_Steppersledge_Switch.Face21]
FEATURE [App::Link] B_Switch_Bracket  label="B-Switch Bracket"
  LinkPlacement = pos=(51.7876,21.8,278.844) rot=(0.707168,-0.707046,3.7e-05;3.14149rad)
  LinkedObject = -> <external Heberteile.FCStd>#Body007
  Placement = pos=(51.7876,21.8,278.844) rot=(0.707168,-0.707046,3.7e-05;3.14149rad)
FEATURE [App::FeaturePython] GroundedJoint001  # Assembly grounded joint (typed FeaturePython)
  ObjectToGround = -> B_Switch_Bracket
  Placement = pos=(51.7876,21.8,278.844) rot=(0.707168,-0.707046,3.7e-05;3.14149rad)
FEATURE [App::FeaturePython] Joint066  label="Abstand"  # Assembly joint (typed FeaturePython)
  Activated = true
  AngleMax = 0
  AngleMin = 0
  Detach1 = false
  Detach2 = false
  Distance = 0
  Distance2 = 0
  EnableAngleMax = false
  EnableAngleMin = false
  EnableLengthMax = false
  EnableLengthMin = false
  JointType = 5 (Distance)
  LengthMax = 0
  LengthMin = 0
  Placement1 = pos=(-13.1,-5.96276,11.0883) rot=(0.57735,0.57735,-0.57735;4.18879rad)
  Reference1 = -> Assembly [Assembly001.B_Switch_Bracket.Hole.Face8,Assembly001.B_Switch_Bracket.Hole.Face8]
  Reference2 = -> Assembly [Assembly001.M2_5x12_Schraube.Face7,Assembly001.M2_5x12_Schraube.Face7]
FEATURE [App::FeaturePython] Joint067  label="ZylindrischeVerbindung002"  # Assembly joint (typed FeaturePython)
  Activated = true
  AngleMax = 0
  AngleMin = 0
  Detach1 = false
  Detach2 = false
  Distance = 0
  Distance2 = 0
  EnableAngleMax = false
  EnableAngleMin = false
  EnableLengthMax = false
  EnableLengthMin = false
  JointType = 2 (Cylindrical)
  LengthMax = 0
  LengthMin = 0
  Placement1 = pos=(2.5,0,14.7) rot=(0.57735,0.57735,0.57735;2.0944rad)
  Reference1 = -> Assembly [Assembly001.B_Switch_Bracket.Hole.Edge106,Assembly001.B_Switch_Bracket.Hole.Edge106]
  Reference2 = -> Assembly [Assembly001.M2_5_Mutter001.Edge27,Assembly001.M2_5_Mutter001.Edge27]
FEATURE [App::FeaturePython] Joint070  label="ZylindrischeVerbindung003"  # Assembly joint (typed FeaturePython)
  Activated = true
  AngleMax = 0
  AngleMin = 0
  Detach1 = false
  Detach2 = false
  Distance = 0
  Distance2 = 0
  EnableAngleMax = false
  EnableAngleMin = false
  EnableLengthMax = false
  EnableLengthMin = false
  JointType = 2 (Cylindrical)
  LengthMax = 0
  LengthMin = 0
  Placement2 = pos=(-13.1,0,5.2) rot=(0,-1,0;1.5708rad)
  Reference1 = -> Assembly [Assembly001.M2_5x12_Schraube001.Edge10,Assembly001.M2_5x12_Schraube001.Edge10]
  Reference2 = -> Assembly [Assembly001.B_Switch_Bracket.Hole.Edge52,Assembly001.B_Switch_Bracket.Hole.Edge52]
FEATURE [App::FeaturePython] Joint071  label="Abstand001"  # Assembly joint (typed FeaturePython)
  Activated = true
  AngleMax = 0
  AngleMin = 0
  Detach1 = false
  Detach2 = false
  Distance = 0
  Distance2 = 0
  EnableAngleMax = false
  EnableAngleMin = false
  EnableLengthMax = false
  EnableLengthMin = false
  JointType = 5 (Distance)
  LengthMax = 0
  LengthMin = 0
  Placement2 = pos=(-13.1,-5.96276,11.0883) rot=(0.57735,0.57735,-0.57735;4.18879rad)
  Reference1 = -> Assembly [Assembly001.M2_5x12_Schraube001.Face7,Assembly001.M2_5x12_Schraube001.Face7]
  Reference2 = -> Assembly [Assembly001.B_Switch_Bracket.Hole.Face8,Assembly001.B_Switch_Bracket.Hole.Face8]
FEATURE [App::FeaturePython] Joint072  label="ZylindrischeVerbindung004"  # Assembly joint (typed FeaturePython)
  Activated = true
  AngleMax = 0
  AngleMin = 0
  Detach1 = false
  Detach2 = false
  Distance = 0
  Distance2 = 0
  EnableAngleMax = false
  EnableAngleMin = false
  EnableLengthMax = false
  EnableLengthMin = false
  JointType = 2 (Cylindrical)
  LengthMax = 0
  LengthMin = 0
  Placement1 = pos=(0,0,-15.75) rot=(0,0,1;0rad)
  Reference1 = -> Assembly [Assembly001.M2_5x12_Schraube001.Edge2,Assembly001.M2_5x12_Schraube001.Edge2]
  Reference2 = -> Assembly [Assembly001.M2_5_Mutter.Edge27,Assembly001.M2_5_Mutter.Edge27]
FEATURE [App::FeaturePython] Joint073  label="Abstand002"  # Assembly joint (typed FeaturePython)
  Activated = true
  AngleMax = 0
  AngleMin = 0
  Detach1 = false
  Detach2 = false
  Distance = 0
  Distance2 = 0
  EnableAngleMax = false
  EnableAngleMin = false
  EnableLengthMax = false
  EnableLengthMin = false
  JointType = 5 (Distance)
  LengthMax = 0
  LengthMin = 0
  Placement1 = pos=(3.6e-15,7.1e-15,9.95) rot=(-0.57735,0.57735,-0.57735;2.0944rad)
  Placement2 = pos=(0,7.1e-15,2) rot=(0,-1,0;3.14159rad)
  Reference1 = -> Assembly [Assembly001.B_Switch_Bracket.Hole.Face30,Assembly001.B_Switch_Bracket.Hole.Face30]
  Reference2 = -> Assembly [Assembly001.M2_5_Mutter.Face2,Assembly001.M2_5_Mutter.Face2]
FEATURE [App::FeaturePython] Joint074  label="Abstand003"  # Assembly joint (typed FeaturePython)
  Activated = true
  AngleMax = 0
  AngleMin = 0
  Detach1 = false
  Detach2 = false
  Distance = 0
  Distance2 = 0
  EnableAngleMax = false
  EnableAngleMin = false
  EnableLengthMax = false
  EnableLengthMin = false
  JointType = 5 (Distance)
  LengthMax = 0
  LengthMin = 0
  Placement1 = pos=(0,-5.68e-14,18.9972) rot=(-0.57735,0.57735,-0.57735;2.0944rad)
  Reference1 = -> Assembly [Assembly001.B_Switch_Bracket.Hole.Face34,Assembly001.B_Switch_Bracket.Hole.Face34]
  Reference2 = -> Assembly [Assembly001.M2_5_Mutter001.Face18,Assembly001.M2_5_Mutter001.Face18]
FEATURE [App::FeaturePython] Joint076  label="Abstand004"  # Assembly joint (typed FeaturePython)
  Activated = true
  AngleMax = 0
  AngleMin = 0
  Detach1 = false
  Detach2 = false
  Distance = 0
  Distance2 = 0
  EnableAngleMax = false
  EnableAngleMin = false
  EnableLengthMax = false
  EnableLengthMin = false
  JointType = 5 (Distance)
  LengthMax = 0
  LengthMin = 0
  Placement1 = pos=(3.2,2.37015,-14.85) rot=(0,1,0;1.5708rad)
  Placement2 = pos=(-6.8,-7.1e-15,10.5856) rot=(0.57735,0.57735,-0.57735;4.18879rad)
  Reference1 = -> Assembly [Assembly001.Microswitch_20mm007.Part__Feature015.Face267,Assembly001.Microswitch_20mm007.Part__Feature015.Face267]
  Reference2 = -> Assembly [Assembly001.B_Switch_Bracket.Hole.Face37,Assembly001.B_Switch_Bracket.Hole.Face37]
FEATURE [App::FeaturePython] Joint077  label="ZylindrischeVerbindung005"  # Assembly joint (typed FeaturePython)
  Activated = true
  AngleMax = 0
  AngleMin = 0
  Detach1 = false
  Detach2 = false
  Distance = 0
  Distance2 = 0
  EnableAngleMax = false
  EnableAngleMin = false
  EnableLengthMax = false
  EnableLengthMin = false
  JointType = 2 (Cylindrical)
  LengthMax = 0
  LengthMin = 0
  Placement1 = pos=(3.2,2.3,-14.85) rot=(0,-1,0;1.5708rad)
  Placement2 = pos=(0,-5.68e-14,-1.26071) rot=(0,0,1;0rad)
  Reference1 = -> Assembly [Assembly001.Microswitch_20mm007.Part__Feature015.Edge720,Assembly001.Microswitch_20mm007.Part__Feature015.Edge720]
  Reference2 = -> Assembly [Assembly001.M2_5x12_Schraube.Edge6,Assembly001.M2_5x12_Schraube.Edge6]
FEATURE [App::FeaturePython] Joint078  label="ZylindrischeVerbindung006"  # Assembly joint (typed FeaturePython)
  Activated = true
  AngleMax = 0
  AngleMin = 0
  Detach1 = false
  Detach2 = false
  Distance = 0
  Distance2 = 0
  EnableAngleMax = false
  EnableAngleMin = false
  EnableLengthMax = false
  EnableLengthMin = false
  JointType = 2 (Cylindrical)
  LengthMax = 0
  LengthMin = 0
  Placement1 = pos=(3.2,2.3,-5.25) rot=(0,-1,0;1.5708rad)
  Placement2 = pos=(-7.1e-15,0,-1.26071) rot=(0,0,1;0rad)
  Reference1 = -> Assembly [Assembly001.Microswitch_20mm007.Part__Feature015.Edge710,Assembly001.Microswitch_20mm007.Part__Feature015.Edge710]
  Reference2 = -> Assembly [Assembly001.M2_5x12_Schraube001.Edge6,Assembly001.M2_5x12_Schraube001.Edge6]
FEATURE [Assembly::JointGroup] Joints001
  Group = -> [GroundedJoint001,Joint066,Joint067,Joint070,Joint071,Joint072,Joint073,Joint074,Joint076,Joint077,Joint078]
FEATURE [Assembly::AssemblyObject] Assembly001  label="Switch-Box"
  Group = -> [Joints001,Microswitch_20mm007,B_Switch_Bracket,M2_5x12_Schraube,M2_5_Mutter,M2_5x12_Schraube001,M2_5_Mutter001,GroundedJoint001,Joint066,Joint067,Joint070,Joint071,Joint072,Joint073,Joint074,Joint076,Joint077,Joint078]
  Origin = -> Origin005
  Placement = pos=(3.8147e-06,-1,0) rot=(0,0,1;0rad)
  Type = Assembly
FEATURE [App::DocumentObjectGroup] Group  label="Components"
  Group = -> [_3HS45_4204S,DM542T_V4_0_,Microswitch_20mm,lifting_jack_assembley,Screw,Washer001,Nut001,Screw003,Screw004,Screw005,Washer,Nut,Assembly001]
FEATURE [App::Link] Microswitch_20mm011  label="Microswitch 001"
  LinkPlacement = pos=(54.0665,25.4004,278.902) rot=(-0.002003,-0.001876,0.999996;1.57097rad)
  LinkedObject = -> Microswitch_20mm007
  Placement = pos=(54.0665,25.4004,278.902) rot=(-0.002003,-0.001876,0.999996;1.57097rad)
FEATURE [App::Link] B_Switch_Bracket001  label="B-Switch Bracket 001"
  LinkPlacement = pos=(51.7876,21.8,278.844) rot=(0.707168,-0.707046,3.7e-05;3.14149rad)
  LinkedObject = -> B_Switch_Bracket
  Placement = pos=(51.7876,21.8,278.844) rot=(0.707168,-0.707046,3.7e-05;3.14149rad)
FEATURE [App::Link] M2_5x12_Schraube008  label="M2.5x16-Schraube003"
  LinkPlacement = pos=(51.8225,34.8981,264.042) rot=(0.014493,0.707079,0.706986;3.17082rad)
  LinkedObject = -> M2_5x12_Schraube
  Placement = pos=(51.8225,34.8981,264.042) rot=(0.014493,0.707079,0.706986;3.17082rad)
FEATURE [App::Link] M2_5_Mutter008  label="M2.5-Mutter009"
  LinkPlacement = pos=(51.7878,19.7993,273.644) rot=(-0.576113,0.577955,0.577981;2.09651rad)
  LinkedObject = -> M2_5_Mutter
  Placement = pos=(51.7878,19.7993,273.644) rot=(-0.576113,0.577955,0.577981;2.09651rad)
FEATURE [App::Link] M2_5x12_Schraube009  label="M2.5x16-Schraube004"
  LinkPlacement = pos=(51.7852,34.8993,273.642) rot=(0,0.707152,0.707062;3.14184rad)
  LinkedObject = -> M2_5x12_Schraube001
  Placement = pos=(51.7852,34.8993,273.642) rot=(0,0.707152,0.707062;3.14184rad)
FEATURE [App::Link] M2_5_Mutter009  label="M2.5-Mutter010"
  LinkPlacement = pos=(51.7873,21.7981,264.144) rot=(0.936105,-0.248607,0.248801;1.6367rad)
  LinkedObject = -> M2_5_Mutter001
  Placement = pos=(51.7873,21.7981,264.144) rot=(0.936105,-0.248607,0.248801;1.6367rad)
FEATURE [Assembly::AssemblyLink] Switch_Top  label="Switch-Top"
  Group = -> [Microswitch_20mm011,B_Switch_Bracket001,M2_5x12_Schraube008,M2_5_Mutter008,M2_5x12_Schraube009,M2_5_Mutter009]
  LinkedObject = -> Assembly001
  Origin = -> Origin006
  Placement = pos=(0.7,-6.00002,27.0002) rot=(0,0,1;0rad)
  Rigid = true
FEATURE [App::Link] Microswitch_20mm012  label="Microswitch 002"
  LinkPlacement = pos=(54.0665,25.4004,278.902) rot=(-0.002003,-0.001876,0.999996;1.57097rad)
  LinkedObject = -> Microswitch_20mm007
  Placement = pos=(54.0665,25.4004,278.902) rot=(-0.002003,-0.001876,0.999996;1.57097rad)
FEATURE [App::Link] B_Switch_Bracket002  label="B-Switch Bracket 002"
  LinkPlacement = pos=(51.7876,21.8,278.844) rot=(0.707168,-0.707046,3.7e-05;3.14149rad)
  LinkedObject = -> B_Switch_Bracket
  Placement = pos=(51.7876,21.8,278.844) rot=(0.707168,-0.707046,3.7e-05;3.14149rad)
FEATURE [App::Link] M2_5x12_Schraube010  label="M2.5x16-Schraube005"
  LinkPlacement = pos=(51.8225,34.8981,264.042) rot=(0.014493,0.707079,0.706986;3.17082rad)
  LinkedObject = -> M2_5x12_Schraube
  Placement = pos=(51.8225,34.8981,264.042) rot=(0.014493,0.707079,0.706986;3.17082rad)
FEATURE [App::Link] M2_5_Mutter010  label="M2.5-Mutter011"
  LinkPlacement = pos=(51.7878,19.7993,273.644) rot=(-0.576113,0.577955,0.577981;2.09651rad)
  LinkedObject = -> M2_5_Mutter
  Placement = pos=(51.7878,19.7993,273.644) rot=(-0.576113,0.577955,0.577981;2.09651rad)
FEATURE [App::Link] M2_5x12_Schraube011  label="M2.5x16-Schraube006"
  LinkPlacement = pos=(51.7852,34.8993,273.642) rot=(0,0.707152,0.707062;3.14184rad)
  LinkedObject = -> M2_5x12_Schraube001
  Placement = pos=(51.7852,34.8993,273.642) rot=(0,0.707152,0.707062;3.14184rad)
FEATURE [App::Link] M2_5_Mutter011  label="M2.5-Mutter012"
  LinkPlacement = pos=(51.7873,21.7981,264.144) rot=(0.936105,-0.248607,0.248801;1.6367rad)
  LinkedObject = -> M2_5_Mutter001
  Placement = pos=(51.7873,21.7981,264.144) rot=(0.936105,-0.248607,0.248801;1.6367rad)
FEATURE [Assembly::AssemblyLink] Switch_Top001  label="Switch-Center"
  Group = -> [Microswitch_20mm012,B_Switch_Bracket002,M2_5x12_Schraube010,M2_5_Mutter010,M2_5x12_Schraube011,M2_5_Mutter011]
  LinkedObject = -> Assembly001
  Origin = -> Origin007
  Placement = pos=(0.8,-5.89597,90) rot=(0,0,1;0rad)
  Rigid = true
FEATURE [App::Link] Microswitch_20mm013  label="Microswitch 003"
  LinkPlacement = pos=(54.0665,25.4004,278.902) rot=(-0.002003,-0.001876,0.999996;1.57097rad)
  LinkedObject = -> Microswitch_20mm007
  Placement = pos=(54.0665,25.4004,278.902) rot=(-0.002003,-0.001876,0.999996;1.57097rad)
FEATURE [App::Link] B_Switch_Bracket003  label="B-Switch Bracket 003"
  LinkPlacement = pos=(51.7876,21.8,278.844) rot=(0.707168,-0.707046,3.7e-05;3.14149rad)
  LinkedObject = -> B_Switch_Bracket
  Placement = pos=(51.7876,21.8,278.844) rot=(0.707168,-0.707046,3.7e-05;3.14149rad)
FEATURE [App::Link] M2_5x12_Schraube012  label="M2.5x16-Schraube007"
  LinkPlacement = pos=(51.8225,34.8981,264.042) rot=(0.014493,0.707079,0.706986;3.17082rad)
  LinkedObject = -> M2_5x12_Schraube
  Placement = pos=(51.8225,34.8981,264.042) rot=(0.014493,0.707079,0.706986;3.17082rad)
FEATURE [App::Link] M2_5_Mutter012  label="M2.5-Mutter013"
  LinkPlacement = pos=(51.7878,19.7993,273.644) rot=(-0.576113,0.577955,0.577981;2.09651rad)
  LinkedObject = -> M2_5_Mutter
  Placement = pos=(51.7878,19.7993,273.644) rot=(-0.576113,0.577955,0.577981;2.09651rad)
FEATURE [App::Link] M2_5x12_Schraube013  label="M2.5x16-Schraube008"
  LinkPlacement = pos=(51.7852,34.8993,273.642) rot=(0,0.707152,0.707062;3.14184rad)
  LinkedObject = -> M2_5x12_Schraube001
  Placement = pos=(51.7852,34.8993,273.642) rot=(0,0.707152,0.707062;3.14184rad)
FEATURE [App::Link] M2_5_Mutter013  label="M2.5-Mutter014"
  LinkPlacement = pos=(51.7873,21.7981,264.144) rot=(0.936105,-0.248607,0.248801;1.6367rad)
  LinkedObject = -> M2_5_Mutter001
  Placement = pos=(51.7873,21.7981,264.144) rot=(0.936105,-0.248607,0.248801;1.6367rad)
FEATURE [Assembly::AssemblyLink] Switch_Top002  label="Switch-Bottom"
  Group = -> [Microswitch_20mm013,B_Switch_Bracket003,M2_5x12_Schraube012,M2_5_Mutter012,M2_5x12_Schraube013,M2_5_Mutter013]
  LinkedObject = -> Assembly001
  Origin = -> Origin008
  Placement = pos=(0.700004,-5.8797,150) rot=(0,0,1;0rad)
  Rigid = true
FEATURE [App::Link] Microswitch_20mm014  label="Microswitch 004"
  LinkPlacement = pos=(54.0665,25.4004,278.902) rot=(-0.002003,-0.001876,0.999996;1.57097rad)
  LinkedObject = -> Microswitch_20mm007
  Placement = pos=(54.0665,25.4004,278.902) rot=(-0.002003,-0.001876,0.999996;1.57097rad)
FEATURE [App::Link] B_Switch_Bracket004  label="B-Switch Bracket 004"
  LinkPlacement = pos=(51.7876,21.8,278.844) rot=(0.707168,-0.707046,3.7e-05;3.14149rad)
  LinkedObject = -> B_Switch_Bracket
  Placement = pos=(51.7876,21.8,278.844) rot=(0.707168,-0.707046,3.7e-05;3.14149rad)
FEATURE [App::Link] M2_5x12_Schraube014  label="M2.5x16-Schraube009"
  LinkPlacement = pos=(51.8225,34.8981,264.042) rot=(0.014493,0.707079,0.706986;3.17082rad)
  LinkedObject = -> M2_5x12_Schraube
  Placement = pos=(51.8225,34.8981,264.042) rot=(0.014493,0.707079,0.706986;3.17082rad)
FEATURE [App::Link] M2_5_Mutter014  label="M2.5-Mutter015"
  LinkPlacement = pos=(51.7878,19.7993,273.644) rot=(-0.576113,0.577955,0.577981;2.09651rad)
  LinkedObject = -> M2_5_Mutter
  Placement = pos=(51.7878,19.7993,273.644) rot=(-0.576113,0.577955,0.577981;2.09651rad)
FEATURE [App::Link] M2_5x12_Schraube015  label="M2.5x16-Schraube010"
  LinkPlacement = pos=(51.7852,34.8993,273.642) rot=(0,0.707152,0.707062;3.14184rad)
  LinkedObject = -> M2_5x12_Schraube001
  Placement = pos=(51.7852,34.8993,273.642) rot=(0,0.707152,0.707062;3.14184rad)
FEATURE [App::Link] M2_5_Mutter015  label="M2.5-Mutter016"
  LinkPlacement = pos=(51.7873,21.7981,264.144) rot=(0.936105,-0.248607,0.248801;1.6367rad)
  LinkedObject = -> M2_5_Mutter001
  Placement = pos=(51.7873,21.7981,264.144) rot=(0.936105,-0.248607,0.248801;1.6367rad)
FEATURE [Assembly::AssemblyLink] Switch_Top003  label="Switch-Down"
  Group = -> [Microswitch_20mm014,B_Switch_Bracket004,M2_5x12_Schraube014,M2_5_Mutter014,M2_5x12_Schraube015,M2_5_Mutter015]
  LinkedObject = -> Assembly001
  Origin = -> Origin009
  Placement = pos=(0.7,-5.87195,274.165) rot=(2.3e-05,-1,0.00015;0rad)
  Rigid = true
FEATURE [App::FeaturePython] Joint080  label="Abstand005"  # Assembly joint (typed FeaturePython)
  Activated = true
  AngleMax = 0
  AngleMin = 0
  Detach1 = false
  Detach2 = false
  Distance = 0
  Distance2 = 0
  EnableAngleMax = false
  EnableAngleMin = false
  EnableLengthMax = false
  EnableLengthMin = false
  JointType = 5 (Distance)
  LengthMax = 0
  LengthMin = 0
  Placement1 = pos=(173.5,59.6438,20.1894) rot=(1,0,0;1.5708rad)
  Placement2 = pos=(-11.1,-5.13756,11.0289) rot=(-0.57735,0.57735,-0.57735;2.0944rad)
  Reference1 = -> Assembly [B_Steppersledge_Switch.Face37,B_Steppersledge_Switch.Vertex72]
  Reference2 = -> Assembly [Switch_Top.B_Switch_Bracket001.Face11,Switch_Top.B_Switch_Bracket001.Vertex44]
FEATURE [App::FeaturePython] Joint081  label="Parallel001"  # Assembly joint (typed FeaturePython)
  Activated = true
  AngleMax = 0
  AngleMin = 0
  Detach1 = false
  Detach2 = false
  Distance = 0
  Distance2 = 0
  EnableAngleMax = false
  EnableAngleMin = false
  EnableLengthMax = false
  EnableLengthMin = false
  JointType = 6 (Parallel)
  LengthMax = 0
  LengthMin = 0
  Placement1 = pos=(-11.1,7,11) rot=(0,0,1;0rad)
  Placement2 = pos=(173.5,59.6438,20.1438) rot=(0.707107,0,0.707107;3.14159rad)
  Reference1 = -> Assembly [Switch_Top.B_Switch_Bracket001.Hole.Edge54,Switch_Top.B_Switch_Bracket001.Hole.Edge54]
  Reference2 = -> Assembly [B_Steppersledge_Switch.Fold013.Edge106,B_Steppersledge_Switch.Fold013.Edge106]
FEATURE [App::FeaturePython] Joint082  label="ZylindrischeVerbindung007"  # Assembly joint (typed FeaturePython)
  Activated = true
  AngleMax = 0
  AngleMin = 0
  Detach1 = false
  Detach2 = false
  Distance = 0
  Distance2 = 0
  EnableAngleMax = false
  EnableAngleMin = false
  EnableLengthMax = false
  EnableLengthMin = false
  JointType = 2 (Cylindrical)
  LengthMax = 0
  LengthMin = 0
  Placement1 = pos=(325.5,58.6438,21.6438) rot=(1,0,0;1.5708rad)
  Placement2 = pos=(0,0,0) rot=(0,-1,0;3.14159rad)
  Reference1 = -> Assembly [B_Steppersledge_Switch.Face34,B_Steppersledge_Switch.Face34]
  Reference2 = -> Assembly [Switch_Top.M2_5x12_Schraube009.Edge12,Switch_Top.M2_5x12_Schraube009.Edge12]
FEATURE [App::FeaturePython] Joint083  label="Abstand006"  # Assembly joint (typed FeaturePython)
  Activated = true
  AngleMax = 0
  AngleMin = 0
  Detach1 = false
  Detach2 = false
  Distance = 0
  Distance2 = 0
  EnableAngleMax = false
  EnableAngleMin = false
  EnableLengthMax = false
  EnableLengthMin = false
  JointType = 5 (Distance)
  LengthMax = 0
  LengthMin = 0
  Placement1 = pos=(-11.1,-5.13756,11.0289) rot=(-0.57735,0.57735,-0.57735;2.0944rad)
  Placement2 = pos=(173.5,59.6438,20.1894) rot=(1,0,0;1.5708rad)
  Reference1 = -> Assembly [Switch_Top001.B_Switch_Bracket002.Hole.Face11,Switch_Top001.B_Switch_Bracket002.Hole.Face11]
  Reference2 = -> Assembly [B_Steppersledge_Switch.Fold013.Face37,B_Steppersledge_Switch.Fold013.Face37]
FEATURE [App::FeaturePython] Joint084  label="Abstand007"  # Assembly joint (typed FeaturePython)
  Activated = true
  AngleMax = 0
  AngleMin = 0
  Detach1 = false
  Detach2 = false
  Distance = 0
  Distance2 = 0
  EnableAngleMax = false
  EnableAngleMin = false
  EnableLengthMax = false
  EnableLengthMin = false
  JointType = 5 (Distance)
  LengthMax = 0
  LengthMin = 0
  Placement1 = pos=(-11.1,-5.13756,11.0289) rot=(-0.57735,0.57735,-0.57735;2.0944rad)
  Placement2 = pos=(173.5,59.6438,20.1894) rot=(1,0,0;1.5708rad)
  Reference1 = -> Assembly [Switch_Top002.B_Switch_Bracket003.Hole.Face11,Switch_Top002.B_Switch_Bracket003.Hole.Face11]
  Reference2 = -> Assembly [B_Steppersledge_Switch.Fold013.Face37,B_Steppersledge_Switch.Fold013.Face37]
FEATURE [App::FeaturePython] Joint085  label="Abstand008"  # Assembly joint (typed FeaturePython)
  Activated = true
  AngleMax = 0
  AngleMin = 0
  Detach1 = false
  Detach2 = false
  Distance = 0
  Distance2 = 0
  EnableAngleMax = false
  EnableAngleMin = false
  EnableLengthMax = false
  EnableLengthMin = false
  JointType = 5 (Distance)
  LengthMax = 0
  LengthMin = 0
  Placement1 = pos=(-11.1,-5.13756,11.0289) rot=(-0.57735,0.57735,-0.57735;2.0944rad)
  Placement2 = pos=(173.5,59.6438,20.1894) rot=(1,0,0;1.5708rad)
  Reference1 = -> Assembly [Switch_Top003.B_Switch_Bracket004.Hole.Face11,Switch_Top003.B_Switch_Bracket004.Hole.Face11]
  Reference2 = -> Assembly [B_Steppersledge_Switch.Fold013.Face37,B_Steppersledge_Switch.Fold013.Face37]
FEATURE [App::Link] M5x20_Schraube  label="M5x20-Schraube001"
  LinkPlacement = pos=(-37.2938,-1.19676e-11,401.144) rot=(-0.707107,0,0.707107;3.14159rad)
  LinkedObject = -> Screw005
  Placement = pos=(-37.2938,-1.19676e-11,401.144) rot=(-0.707107,0,0.707107;3.14159rad)
FEATURE [App::Link] M5x20_Schraube001  label="M5x20-Schraube002"
  LinkPlacement = pos=(37.2938,-1.62805e-11,401.144) rot=(0.707107,0,0.707107;3.14159rad)
  LinkedObject = -> Screw005
  Placement = pos=(37.2938,-1.62805e-11,401.144) rot=(0.707107,0,0.707107;3.14159rad)
FEATURE [App::Link] M5_Scheibe008  label="M5-Scheibe001"
  LinkPlacement = pos=(-36.2938,-1.19644e-11,401.144) rot=(-0.707107,0,0.707107;3.14159rad)
  LinkedObject = -> Washer
  Placement = pos=(-36.2938,-1.19644e-11,401.144) rot=(-0.707107,0,0.707107;3.14159rad)
FEATURE [App::Link] M5_Scheibe009  label="M5-Scheibe002"
  LinkPlacement = pos=(36.2938,-1.62842e-11,401.144) rot=(0.707107,0,0.707107;3.14159rad)
  LinkedObject = -> Washer
  Placement = pos=(36.2938,-1.62842e-11,401.144) rot=(0.707107,0,0.707107;3.14159rad)
FEATURE [App::FeaturePython] Joint086  label="Gleitverbindung054"  # Assembly joint (typed FeaturePython)
  Activated = true
  AngleMax = 0
  AngleMin = 0
  Detach1 = false
  Detach2 = false
  Distance = 0
  Distance2 = 0
  EnableAngleMax = false
  EnableAngleMin = false
  EnableLengthMax = false
  EnableLengthMin = false
  JointType = 3 (Slider)
  LengthMax = 0
  LengthMin = 0
  Offset1 = pos=(0,1,0) rot=(0,0,1;0rad)
  Placement1 = pos=(0,0,6.3) rot=(0,0,1;0rad)
  Reference1 = -> Assembly [B_SlideBearing.Fillet.Edge14,B_SlideBearing.Fillet.Edge14]
  Reference2 = -> Assembly [M5_Scheibe008.Edge5,M5_Scheibe008.Edge5]
FEATURE [App::FeaturePython] Joint087  label="ZylindrischeVerbindung008"  # Assembly joint (typed FeaturePython)
  Activated = true
  AngleMax = 0
  AngleMin = 0
  Detach1 = false
  Detach2 = false
  Distance = 0
  Distance2 = 0
  EnableAngleMax = false
  EnableAngleMin = false
  EnableLengthMax = false
  EnableLengthMin = false
  JointType = 2 (Cylindrical)
  LengthMax = 0
  LengthMin = 0
  Placement1 = pos=(0,0,1) rot=(0,0,1;0rad)
  Reference1 = -> Assembly [M5_Scheibe008.Edge1,M5_Scheibe008.Edge1]
  Reference2 = -> Assembly [M5x20_Schraube.Edge50,M5x20_Schraube.Edge50]
FEATURE [App::FeaturePython] Joint088  label="Gleitverbindung055"  # Assembly joint (typed FeaturePython)
  Activated = true
  AngleMax = 0
  AngleMin = 0
  Detach1 = false
  Detach2 = false
  Distance = 0
  Distance2 = 0
  EnableAngleMax = false
  EnableAngleMin = false
  EnableLengthMax = false
  EnableLengthMin = false
  JointType = 3 (Slider)
  LengthMax = 0
  LengthMin = 0
  Offset1 = pos=(0,1,0) rot=(0,0,1;0rad)
  Placement1 = pos=(0,0,6.3) rot=(0,0,1;0rad)
  Reference1 = -> Assembly [B_Slide_Bearing_w__Indicator.Pad006.Edge48,B_Slide_Bearing_w__Indicator.Pad006.Edge48]
  Reference2 = -> Assembly [M5_Scheibe009.Edge5,M5_Scheibe009.Edge5]
FEATURE [App::FeaturePython] Joint089  label="ZylindrischeVerbindung009"  # Assembly joint (typed FeaturePython)
  Activated = true
  AngleMax = 0
  AngleMin = 0
  Detach1 = false
  Detach2 = false
  Distance = 0
  Distance2 = 0
  EnableAngleMax = false
  EnableAngleMin = false
  EnableLengthMax = false
  EnableLengthMin = false
  JointType = 2 (Cylindrical)
  LengthMax = 0
  LengthMin = 0
  Placement1 = pos=(0,0,1) rot=(0,0,1;0rad)
  Reference1 = -> Assembly [M5_Scheibe009.Edge1,M5_Scheibe009.Edge1]
  Reference2 = -> Assembly [M5x20_Schraube001.Edge50,M5x20_Schraube001.Edge50]
FEATURE [Assembly::JointGroup] Joints
  Group = -> [GroundedJoint,Joint,Joint001,Joint002,Joint003,Joint004,Joint005,Joint006,Joint007,Joint008,Joint009,Joint012,Joint013,Joint014,Joint015,Joint016,Joint017,Joint018,Joint019,Joint020,Joint021,Joint052,Joint053,Joint056,Joint057,Joint061,Joint080,Joint081,Joint082,Joint083,Joint084,Joint085,Joint086,Joint087,Joint088,Joint089]
FEATURE [Assembly::AssemblyObject] Assembly  label="Mover"
  Group = -> [Joints,B_Steppersledge_basic,B_Steppersledge_Switch,B_SlideBearing,B_Slide_Bearing_Wascher,B_Sheetwasher,B_Slide_Bearing_w__Indicator,B_Slide_Bearing_Wascher001,B_Mount_Washer,_3HS45_4204S006,GroundedJoint,Joint,Joint001,Joint002,Joint003,Joint004,Joint005,M5x12_Schraube,M5x12_Schraube001,M5x12_Schraube002,M5x12_Schraube003,M5_Scheibe,M5_Scheibe002,M5_Scheibe001,M5_Scheibe003,M5_Mutter,+44 more]
  Origin = -> Origin001
  Type = Assembly

RESOLVED EXTERNAL PARTS (link-assembly join: the EXTERNAL_REF files above that resolve inside this repo's crawl, each included once):
---- part Heberteile.FCStd = doc fcstd_8dd0abafd35a (117330 chars; too large to inline — full recipe in that document) ----
